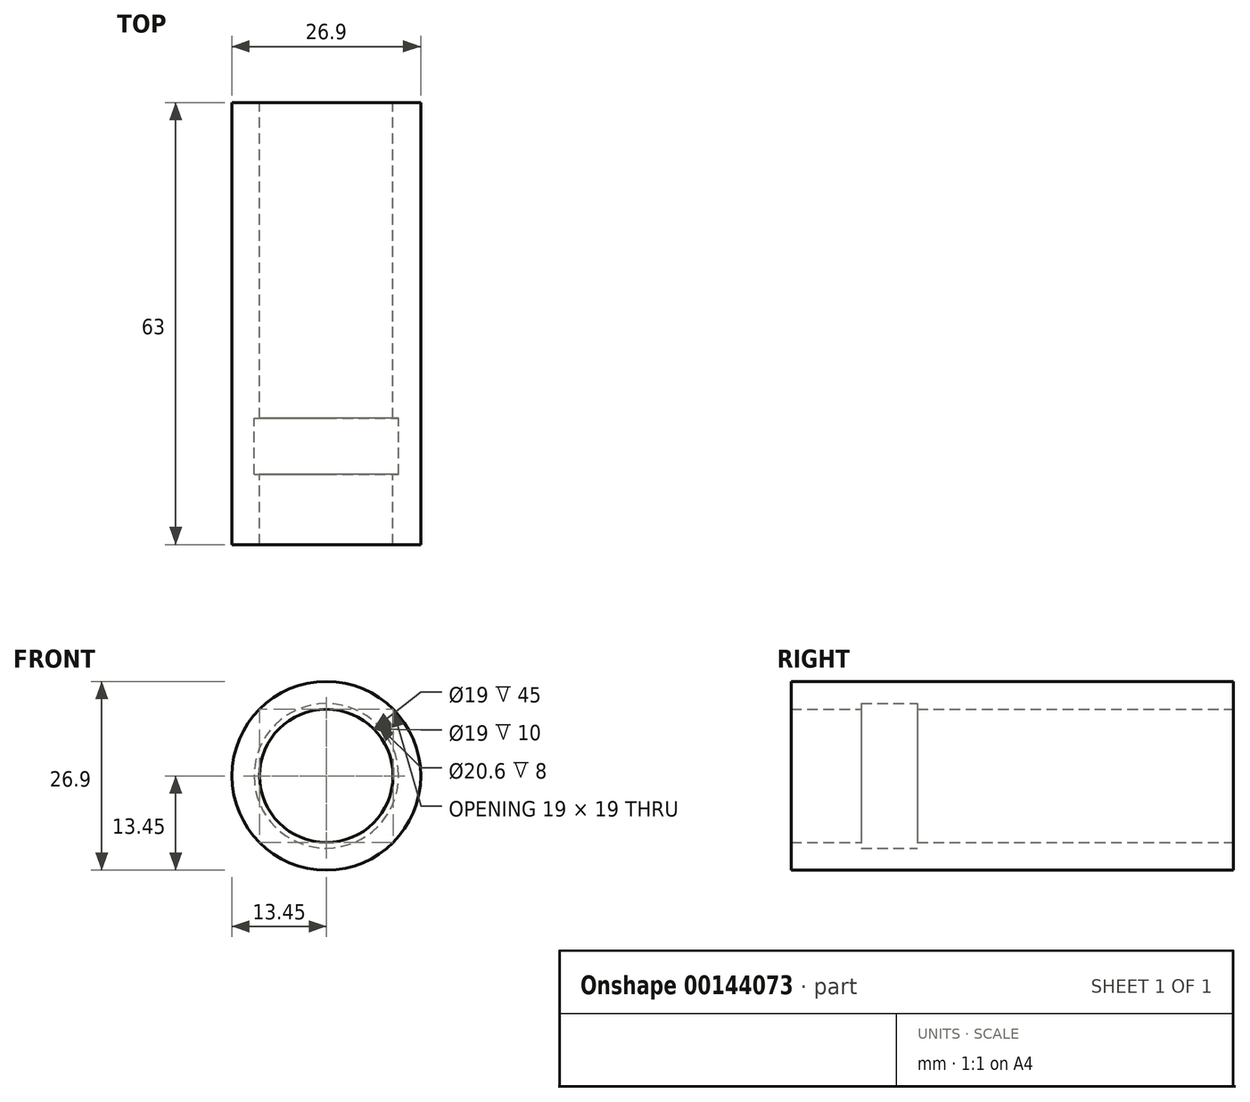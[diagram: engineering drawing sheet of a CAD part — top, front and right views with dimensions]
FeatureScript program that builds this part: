
annotation { "Feature Type Name" : "Feature", "Feature Type Description" : "" }
export const myFeature = defineFeature(function(context is Context, id is Id, definition is map)
    precondition{}
    {
        {
            var Q0;
            Q0=qCreatedBy(makeId("Front.planeOp"),FACE);
            var sketch = newSketch(context, id + "F0", { "sketchPlane" : qUnion([Q0])});
            skCircle(sketch, "E0", {"center": v(0, 0) * mm, "radius": 13.45 * mm});
            skCircle(sketch, "E1", {"center": v(0, 0) * mm, "radius": 9.5 * mm});
            skSolve(sketch);
        }
        {
            var Q0;
            Q0=makeQuery(id+"F0.imprint","IMPRINT",FACE,{"disambiguationData":[TD([[makeQuery(id+"F0.imprint","IMPRINT",EDGE,{"derivedFrom":sQuery(id+"F0.wireOp",EDGE,"E0")}),1.0]])]});
            extrude(context, id + "F1", {"entities" : qUnion([Q0]), "depth" : 63 * mm});
        }
        {
            var Q0;
            Q0=qCreatedBy(makeId("Right.planeOp"),FACE);
            var sketch = newSketch(context, id + "F2", { "sketchPlane" : qUnion([Q0])});
            skLineSegment(sketch, "E2", {"start": v(0, 0) * mm, "end": v(-63, 0) * mm, "construction": true});
            skLineSegment(sketch, "E3.0", {"start": v(-63, -9.5) * mm, "end": v(-63, 9.5) * mm, "construction": true});
            skLineSegment(sketch, "E4", {"start": v(-63, 9.5) * mm, "end": v(-53, 9.5) * mm, "construction": true});
            skLineSegment(sketch, "E5", {"start": v(-45, 9.5) * mm, "end": v(-53, 9.5) * mm});
            skLineSegment(sketch, "E6", {"start": v(-63, 9.5) * mm, "end": v(-63, 11.71) * mm, "construction": true});
            skLineSegment(sketch, "E7", {"start": v(-45, 9.5) * mm, "end": v(-45, 10.3) * mm});
            skLineSegment(sketch, "E8", {"start": v(-45, 10.3) * mm, "end": v(-53, 10.3) * mm});
            skLineSegment(sketch, "E9", {"start": v(-53, 10.3) * mm, "end": v(-53, 9.5) * mm});
            skLineSegment(sketch, "E10", {"start": v(-53, 10.3) * mm, "end": v(-63, 10.3) * mm, "construction": true});
            skPoint(sketch, "E10.endSnap0", {"position": v(-63, 10.6) * mm});
            skLineSegment(sketch, "E11", {"start": v(-63, 9.5) * mm, "end": v(-63, 10.3) * mm, "construction": true});
            skSolve(sketch);
        }
        {
            var Q0;
            Q0 = qSketchRegion(id + "F2", true);
            var Q1;
            Q1=sQuery(id+"F2.wireOp",EDGE,"E2");
            revolve(context, id + "F3", {"operationType" : NewBodyOperationType.REMOVE, "entities" : qUnion([Q0]), "axis" : qUnion([Q1]), "revolveType" : RevolveType.FULL});
        }
    });
